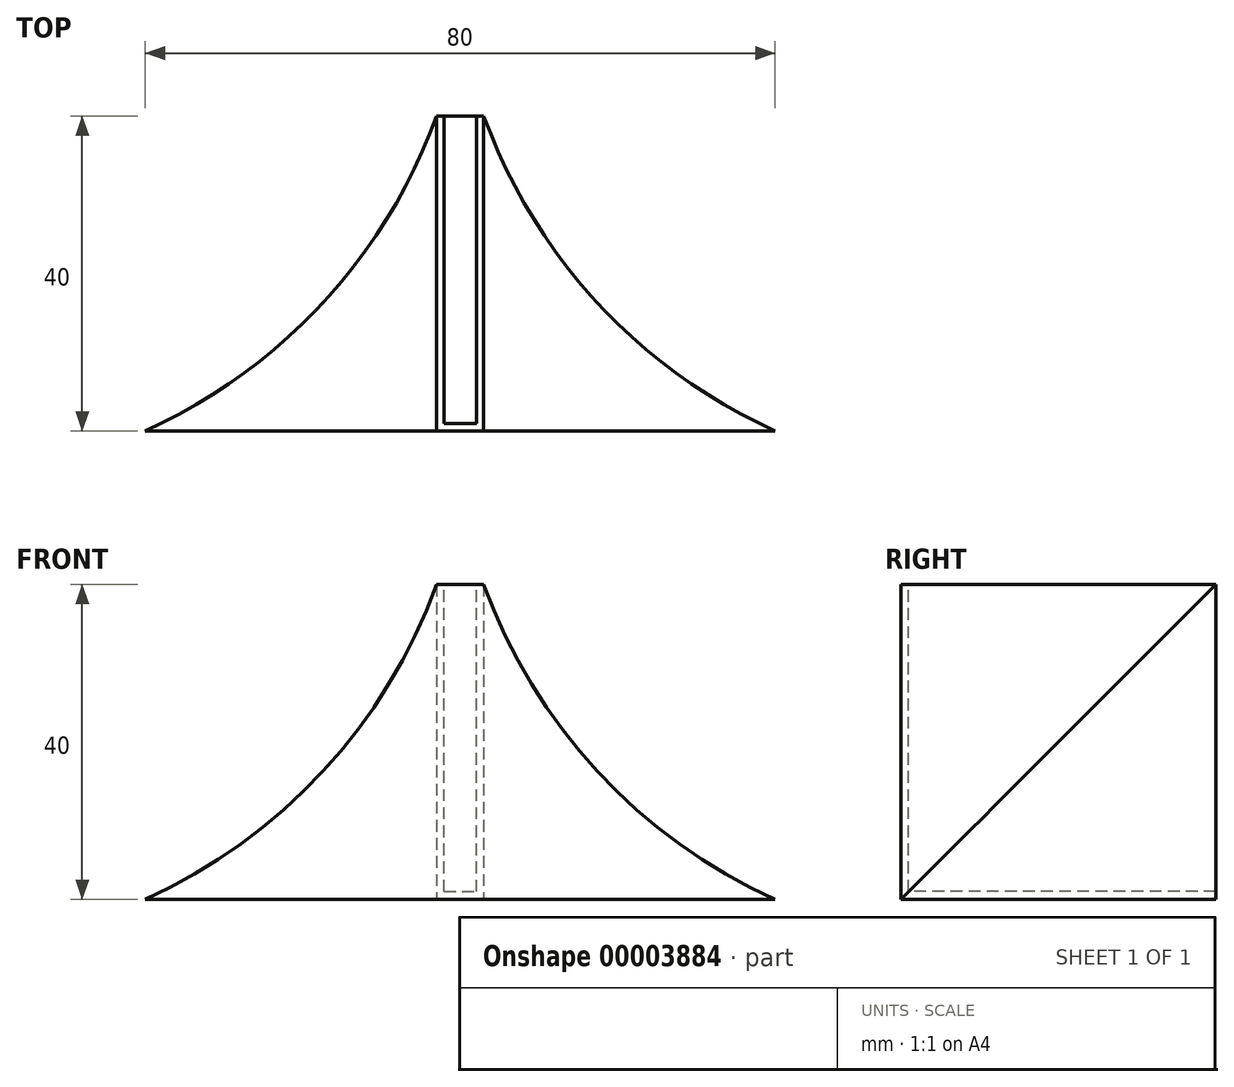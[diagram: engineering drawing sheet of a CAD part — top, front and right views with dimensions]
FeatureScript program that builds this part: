
annotation { "Feature Type Name" : "Feature", "Feature Type Description" : "" }
export const myFeature = defineFeature(function(context is Context, id is Id, definition is map)
    precondition{}
    {
        {
            var Q0;
            Q0=qCreatedBy(makeId("Top.planeOp"),FACE);
            var sketch = newSketch(context, id + "F0", { "sketchPlane" : qUnion([Q0])});
            skLineSegment(sketch, "E0", {"start": v(0, 40) * mm, "end": v(0, 0) * mm, "construction": true});
            skLineSegment(sketch, "E1", {"start": v(0, 0) * mm, "end": v(40, 0) * mm});
            skLineSegment(sketch, "E2", {"start": v(0, 40) * mm, "end": v(3, 40) * mm});
            skArc(sketch, "E3", {"start": v(3, 40) * mm, "mid": v(17.45, 16.25) * mm, "end": v(40, 0) * mm});
            skLineSegment(sketch, "E4.0.MirrorCS", {"start": v(0, 0) * mm, "end": v(-40, 0) * mm});
            skLineSegment(sketch, "E4.1.MirrorCS", {"start": v(0, 40) * mm, "end": v(-3, 40) * mm});
            skArc(sketch, "E4.2.MirrorCS", {"start": v(-3, 40) * mm, "mid": v(-17.45, 16.25) * mm, "end": v(-40, 0) * mm});
            skSolve(sketch);
        }
        {
            var Q0;
            Q0=makeQuery(id+"F0.imprint","IMPRINT",FACE,{"disambiguationData":[TD([[makeQuery(id+"F0.imprint","IMPRINT",EDGE,{"derivedFrom":sQuery(id+"F0.wireOp",EDGE,"E2")}),-1.0]])]});
            extrude(context, id + "F1", {"entities" : qUnion([Q0]), "depth" : 40 * mm});
        }
        {
            var Q0;
            Q0=makeQuery(id+"F1.opExtrude","SWEPT_FACE",FACE,{"disambiguationData":[OSD([sQuery(id+"F0.wireOp",EDGE,"E4.0.MirrorCS")])]});
            var sketch = newSketch(context, id + "F2", { "sketchPlane" : qUnion([Q0])});
            skLineSegment(sketch, "E5", {"start": v(0, 40) * mm, "end": v(3, 40) * mm});
            skArc(sketch, "E6", {"start": v(3, 40) * mm, "mid": v(17.45, 16.25) * mm, "end": v(40, 0) * mm});
            skLineSegment(sketch, "E7", {"start": v(-40, 0) * mm, "end": v(-40, 40) * mm});
            skLineSegment(sketch, "E8", {"start": v(-40, 40) * mm, "end": v(40, 40) * mm});
            skLineSegment(sketch, "E9", {"start": v(40, 40) * mm, "end": v(40, 0) * mm});
            skLineSegment(sketch, "E10", {"start": v(0, 40) * mm, "end": v(0, 0) * mm, "construction": true});
            skArc(sketch, "E11.0.MirrorCS", {"start": v(-3, 40) * mm, "mid": v(-17.45, 16.25) * mm, "end": v(-40, 0) * mm});
            skSolve(sketch);
        }
        {
            var Q0;
            {var subQ2=sQuery(id+"F2.wireOp",EDGE,"E6");Q0=makeQuery(id+"F2.imprint","IMPRINT",FACE,{"disambiguationData":[TD([[makeQuery(id+"F2.imprint","IMPRINT",EDGE,{"derivedFrom":subQ2}),1.0]])]});}
            var Q1;
            {var subQ2=sQuery(id+"F2.wireOp",EDGE,"E7");Q1=makeQuery(id+"F2.imprint","IMPRINT",FACE,{"disambiguationData":[TD([[makeQuery(id+"F2.imprint","IMPRINT",EDGE,{"derivedFrom":subQ2}),1.0]])]});}
            extrude(context, id + "F3", {"entities" : qUnion([Q0, Q1]), "operationType" : NewBodyOperationType.REMOVE, "endBound" : BoundingType.THROUGH_ALL, "oppositeDirection" : true, "depth" : 25 * mm});
        }
        {
            var Q0;
            Q0=makeQuery(id+"F1.opExtrude","CAP_FACE",FACE,{"disambiguationData":[OSD([sQuery(id+"F0.wireOp",EDGE,"E2"),sQuery(id+"F0.wireOp",EDGE,"E3"),sQuery(id+"F0.wireOp",EDGE,"E4.0.MirrorCS"),sQuery(id+"F0.wireOp",EDGE,"E4.2.MirrorCS")])],"isStart":false});
            var sketch = newSketch(context, id + "F4", { "sketchPlane" : qUnion([Q0])});
            skLineSegment(sketch, "E12", {"start": v(0, 0) * mm, "end": v(0, 40) * mm, "construction": true});
            skLineSegment(sketch, "E13", {"start": v(0, 40) * mm, "end": v(2.05, 40) * mm});
            skLineSegment(sketch, "E14", {"start": v(2.05, 40) * mm, "end": v(2.05, 0.96) * mm});
            skLineSegment(sketch, "E15", {"start": v(2.05, 0.96) * mm, "end": v(0, 0.96) * mm});
            skLineSegment(sketch, "E16.0.MirrorCS", {"start": v(-2.05, 0.96) * mm, "end": v(0, 0.96) * mm});
            skLineSegment(sketch, "E16.1.MirrorCS", {"start": v(0, 40) * mm, "end": v(-2.05, 40) * mm});
            skLineSegment(sketch, "E16.2.MirrorCS", {"start": v(-2.05, 40) * mm, "end": v(-2.05, 0.96) * mm});
            skSolve(sketch);
        }
        {
            var Q0;
            Q0 = qSketchRegion(id + "F4", true);
            extrude(context, id + "F5", {"entities" : qUnion([Q0]), "operationType" : NewBodyOperationType.REMOVE, "oppositeDirection" : true, "depth" : 39 * mm});
        }
    });
